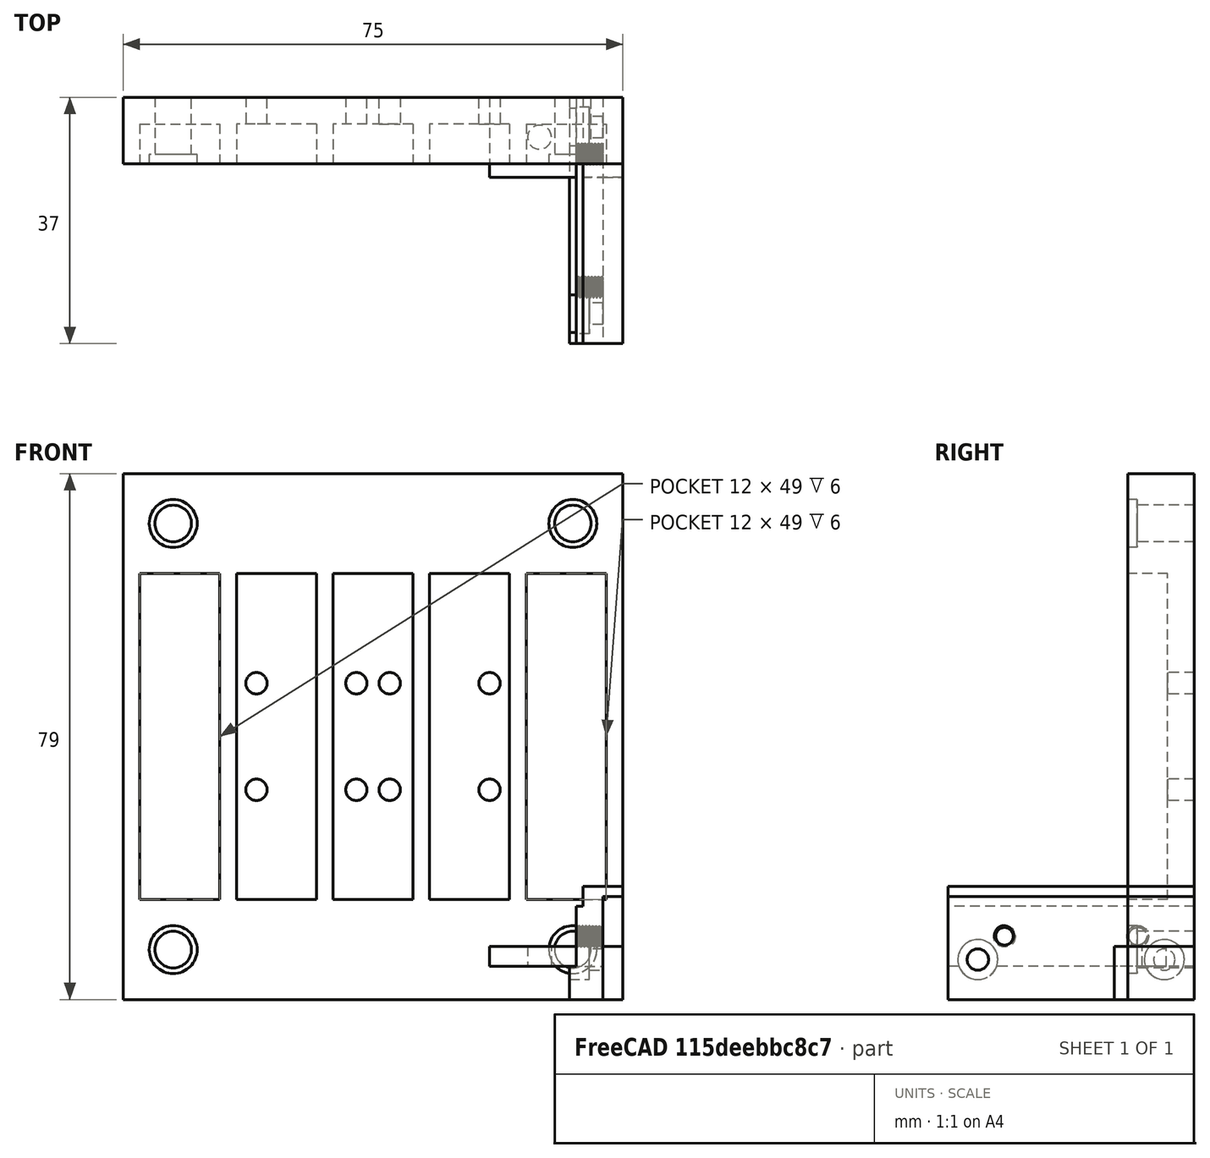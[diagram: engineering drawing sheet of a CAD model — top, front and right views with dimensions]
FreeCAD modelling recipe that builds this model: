
FCSTD DOCUMENT  (FreeCAD 0.20R29410 (Git))
Label: y_rail
License: All rights reserved
LicenseURL: http://en.wikipedia.org/wiki/All_rights_reserved
objects: Sketcher::SketchObject×12, PartDesign::Pocket×7, PartDesign::Pad×5, PartDesign::Body×3, Mesh::Feature×3, Part::FeaturePython×2, Part::Cut×2, PartDesign::Mirrored×1, PartDesign::LinearPattern×1
note: 45 computed .brp shape members not serialized (recipe doc carries the construction recipe); baked Part::Feature solids carry a one-line shape summary decoded from their .brp

FEATURE [Sketcher::SketchObject] Sketch
  FullyConstrained = true
  MapMode = 5
  Placement = pos=(0,0,0) rot=(1,0,0;1.5708rad)
  Support = -> [XZ_Plane]
  sketch-geometry (10):
    g0: LineSegment StartX=0 StartY=17 StartZ=0 EndX=0 EndY=15.5 EndZ=0
    g1: LineSegment StartX=0 StartY=15.5 StartZ=0 EndX=-3 EndY=15.5 EndZ=0
    g2: LineSegment StartX=-3 StartY=15.5 StartZ=0 EndX=-3 EndY=0 EndZ=0
    g3: LineSegment StartX=-3 StartY=0 StartZ=0 EndX=-8 EndY=0 EndZ=0
    g4: LineSegment StartX=-8 StartY=0 StartZ=0 EndX=-8 EndY=5 EndZ=0
    g5: LineSegment StartX=-8 StartY=5 StartZ=0 EndX=-7 EndY=5 EndZ=0
    g6: LineSegment StartX=-7 StartY=5 StartZ=0 EndX=-7 EndY=14 EndZ=0
    g7: LineSegment StartX=-7 StartY=14 StartZ=0 EndX=-6 EndY=14 EndZ=0
    g8: LineSegment StartX=-6 StartY=14 StartZ=0 EndX=-6 EndY=17 EndZ=0
    g9: LineSegment StartX=-6 StartY=17 StartZ=0 EndX=0 EndY=17 EndZ=0
  constraints (30):
    c: PointOnObject(g0,g-2)
    c: Vertical(g0)
    c: Coincident(g1,g0)
    c: Horizontal(g1)
    c: Coincident(g2,g1)
    c: PointOnObject(g2,g-1)
    c: Vertical(g2)
    c: Coincident(g3,g2)
    c: PointOnObject(g3,g-1)
    c: Coincident(g4,g3)
    c: Vertical(g4)
    c: Coincident(g5,g4)
    c: Horizontal(g5)
    c: Coincident(g6,g5)
    c: Vertical(g6)
    c: Coincident(g7,g6)
    c: Coincident(g8,g7)
    c: Vertical(g8)
    c: Coincident(g9,g8)
    c: Coincident(g9,g0)
    c: Horizontal(g9)
    c: DistanceY(g8,g8) = 3
    c: DistanceY(g6,g6) = 9
    c: DistanceY(g4,g4) = 5
    c: Horizontal(g7)
    c: Equal(g7,g5)
    c: DistanceX(g7,g7) = 1
    c: DistanceX(g9,g9) = 6
    c: DistanceX(g1,g1) = 3
    c: DistanceY(g0,g0) = 1.5
FEATURE [PartDesign::Pad] Pad
  Direction = (0,-1,-2e-16)
  Length = 37
  Length2 = 10
  Placement = pos=(0,0,0) rot=(1,0,0;1.5708rad)
  Profile = -> Sketch
  ReferenceAxis = -> Sketch [N_Axis]
  Type = 0
FEATURE [Sketcher::SketchObject] Sketch001
  ExternalGeometry = -> [Pad]
  FullyConstrained = true
  MapMode = 5
  Placement = pos=(-7,0,0) rot=(0.707107,0,-0.707107;3.14159rad)
  Support = -> [Pad]
  sketch-geometry (7):
    g0: Circle CenterX=-9.5 CenterY=28.5 CenterZ=0 NormalX=0 NormalY=0 NormalZ=1 AngleXU=0 Radius=1.25
    g1: Circle CenterX=-9.5 CenterY=8.5 CenterZ=0 NormalX=0 NormalY=0 NormalZ=1 AngleXU=0 Radius=1.25
    g2: LineSegment StartX=-9.5 StartY=28.5 StartZ=0 EndX=-9.5 EndY=8.5 EndZ=0
    g3: GeomPoint X=-9.5 Y=18.5 Z=0
    g4: LineSegment StartX=-14 StartY=37 StartZ=0 EndX=-5 EndY=0 EndZ=0
    g5: LineSegment StartX=-14 StartY=0 StartZ=0 EndX=-5 EndY=37 EndZ=0
    g6: GeomPoint X=-9.5 Y=18.5 Z=0
  constraints (14):
    c: Equal(g0,g1)
    c: Vertical(g0,g1)
    c: Coincident(g2,g0)
    c: Coincident(g2,g1)
    c: DistanceY(g2,g2) = 20
    c: Symmetric(g0,g1,g3)
    c: Coincident(g4,g-3)
    c: Coincident(g5,g-3)
    c: PointOnObject(g6,g5)
    c: PointOnObject(g6,g4)
    c: Coincident(g6,g3)
    c: Diameter(g0) = 2.5
    c: Coincident(g5,g-4)
    c: Coincident(g4,g-4)
FEATURE [PartDesign::Pocket] Pocket  label="table_handle_hole"
  BaseFeature = -> Pad
  Direction = (1,0,2e-16)
  Length = 5
  Length2 = 5
  Placement = pos=(0,0,0) rot=(1,0,0;1.5708rad)
  Profile = -> Sketch001
  ReferenceAxis = -> Sketch001 [N_Axis]
  Type = 1
FEATURE [Sketcher::SketchObject] Sketch002
  ExternalGeometry = -> [Pocket]
  FullyConstrained = true
  MapMode = 5
  Placement = pos=(-8,0,0) rot=(0.707107,0,-0.707107;3.14159rad)
  Support = -> [Pocket]
  sketch-geometry (5):
    g0: Circle CenterX=-6 CenterY=32.5 CenterZ=0 NormalX=0 NormalY=0 NormalZ=1 AngleXU=0 Radius=3
    g1: Circle CenterX=-6 CenterY=4.5 CenterZ=0 NormalX=0 NormalY=0 NormalZ=1 AngleXU=0 Radius=3
    g2: LineSegment StartX=-6 StartY=32.5 StartZ=0 EndX=-6 EndY=4.5 EndZ=0
    g3: GeomPoint X=-6 Y=18.5 Z=0
    g4: GeomPoint X=-5 Y=18.5 Z=0
  constraints (10):
    c: Equal(g0,g1)
    c: Coincident(g2,g0)
    c: Coincident(g2,g1)
    c: Vertical(g2)
    c: DistanceY(g2,g2) = 28
    c: Diameter(g1) = 6
    c: Symmetric(g1,g0,g3)
    c: Symmetric(g-4,g-4,g4)
    c: Horizontal(g4,g3)
    c: DistanceX(g-3,g3) = 9.5
FEATURE [PartDesign::Pocket] Pocket001  label="Y_rail_to_guide_head"
  BaseFeature = -> Pocket
  Direction = (1,0,2e-16)
  Length = 3
  Length2 = 5
  Placement = pos=(0,0,0) rot=(1,0,0;1.5708rad)
  Profile = -> Sketch002
  ReferenceAxis = -> Sketch002 [N_Axis]
  Type = 0
FEATURE [Sketcher::SketchObject] Sketch003
  ExternalGeometry = -> [Pocket001]
  FullyConstrained = true
  MapMode = 5
  Placement = pos=(-5,0,-1e-15) rot=(0.707107,0,-0.707107;3.14159rad)
  Support = -> [Pocket001]
  sketch-geometry (2):
    g0: Circle CenterX=-6 CenterY=32.5 CenterZ=0 NormalX=0 NormalY=0 NormalZ=1 AngleXU=0 Radius=1.6
    g1: Circle CenterX=-6 CenterY=4.5 CenterZ=0 NormalX=0 NormalY=0 NormalZ=1 AngleXU=0 Radius=1.6
  constraints (4):
    c: Coincident(g0,g-3)
    c: Coincident(g1,g-4)
    c: Equal(g0,g1)
    c: Diameter(g0) = 3.2
FEATURE [PartDesign::Pocket] Pocket002  label="Y_rail_to_guide"
  BaseFeature = -> Pocket001
  Direction = (1,0,2e-16)
  Length = 5
  Length2 = 5
  Placement = pos=(0,0,0) rot=(1,0,0;1.5708rad)
  Profile = -> Sketch003
  ReferenceAxis = -> Sketch003 [N_Axis]
  Type = 1
FEATURE [PartDesign::Body] Body  label="Y_rail_holder"
  Group = -> [Sketch,Pad,Sketch001,Pocket,Sketch002,Pocket001,Sketch003,Pocket002]
  Origin = -> Origin
  Tip = -> Pocket002
FEATURE [Part::FeaturePython] ScrewTap  label="M3x5-ScrewTap"  # Fasteners workbench fastener (typed FeaturePython)
  Placement = pos=(-7,-8.5,9.5) rot=(0,-1,0;1.5708rad)
  baseObject = -> Body [Edge47]
  diameter = 4
  diameterCustom = 6
  invert = false
  leftHanded = false
  length = 5
  matchOuter = false
  offset = 0
  pitchCustom = 1
  thread = true
FEATURE [Part::FeaturePython] ScrewTap001  label="M3x5-ScrewTap001"  # Fasteners workbench fastener (typed FeaturePython)
  Placement = pos=(-7,-28.5,9.5) rot=(0,-1,0;1.5708rad)
  baseObject = -> Body [Edge46]
  diameter = 4
  diameterCustom = 6
  invert = false
  leftHanded = false
  length = 5
  matchOuter = false
  offset = 0
  pitchCustom = 1
  thread = true
FEATURE [Part::Cut] Cut
  Base = -> Body
  Tool = -> ScrewTap
FEATURE [Part::Cut] Cut001  label="Y_holder_screwed"
  Base = -> Cut
  Tool = -> ScrewTap001
FEATURE [Mesh::Feature] Mesh  label="Y_holder_screwed (Meshed)"
FEATURE [Sketcher::SketchObject] Sketch008
  FullyConstrained = true
  MapMode = 5
  Placement = pos=(0,0,0) rot=(1,0,0;1.5708rad)
  Support = -> [XZ_Plane003]
  sketch-geometry (4):
    g0: LineSegment StartX=0 StartY=0 StartZ=0 EndX=-75 EndY=0 EndZ=0
    g1: LineSegment StartX=-75 StartY=0 StartZ=0 EndX=-75 EndY=79 EndZ=0
    g2: LineSegment StartX=-75 StartY=79 StartZ=0 EndX=0 EndY=79 EndZ=0
    g3: LineSegment StartX=0 StartY=79 StartZ=0 EndX=0 EndY=0 EndZ=0
  constraints (11):
    c: Coincident(g0,g1)
    c: Coincident(g1,g2)
    c: Coincident(g2,g3)
    c: Coincident(g3,g0)
    c: Horizontal(g0)
    c: Horizontal(g2)
    c: Vertical(g1)
    c: Vertical(g3)
    c: Coincident(g0,g-1)
    c: DistanceX(g2,g2) = 75
    c: DistanceY(g1,g1) = 79
FEATURE [PartDesign::Pad] Pad003  label="to_table_plate001"
  Direction = (0,-1,-2e-16)
  Length = 4
  Length2 = 10
  Placement = pos=(0,0,0) rot=(1,0,0;1.5708rad)
  Profile = -> Sketch008
  ReferenceAxis = -> Sketch008 [N_Axis]
  Type = 0
FEATURE [Sketcher::SketchObject] Sketch009
  ExternalGeometry = -> [Pad003]
  FullyConstrained = true
  MapMode = 5
  Placement = pos=(0,-4,-9e-16) rot=(1,0,0;1.5708rad)
  Support = -> [Pad003]
  sketch-geometry (8):
    g0: LineSegment StartX=-75 StartY=79 StartZ=0 EndX=0 EndY=79 EndZ=0
    g1: LineSegment StartX=0 StartY=79 StartZ=0 EndX=0 EndY=64 EndZ=0
    g2: LineSegment StartX=0 StartY=64 StartZ=0 EndX=-75 EndY=64 EndZ=0
    g3: LineSegment StartX=-75 StartY=64 StartZ=0 EndX=-75 EndY=79 EndZ=0
    g4: LineSegment StartX=-75 StartY=15 StartZ=0 EndX=0 EndY=15 EndZ=0
    g5: LineSegment StartX=0 StartY=15 StartZ=0 EndX=0 EndY=0 EndZ=0
    g6: LineSegment StartX=0 StartY=0 StartZ=0 EndX=-75 EndY=0 EndZ=0
    g7: LineSegment StartX=-75 StartY=0 StartZ=0 EndX=-75 EndY=15 EndZ=0
  constraints (20):
    c: Coincident(g0,g1)
    c: Coincident(g1,g2)
    c: Coincident(g2,g3)
    c: Coincident(g3,g0)
    c: Horizontal(g2)
    c: Vertical(g1)
    c: Vertical(g3)
    c: Coincident(g4,g5)
    c: Coincident(g5,g6)
    c: Coincident(g6,g7)
    c: Coincident(g7,g4)
    c: Horizontal(g4)
    c: Vertical(g5)
    c: Vertical(g7)
    c: Equal(g7,g3)
    c: Coincident(g0,g-3)
    c: Coincident(g0,g-3)
    c: Coincident(g6,g-4)
    c: Coincident(g5,g-4)
    c: DistanceY(g3,g3) = 15
FEATURE [PartDesign::Pad] Pad004  label="to_table_up"
  BaseFeature = -> Pad003
  Direction = (0,-1,-2e-16)
  Length = 6
  Length2 = 10
  Placement = pos=(0,0,0) rot=(1,0,0;1.5708rad)
  Profile = -> Sketch009
  ReferenceAxis = -> Sketch009 [N_Axis]
  Type = 0
FEATURE [Sketcher::SketchObject] Sketch010
  ExternalGeometry = -> [Pad004]
  FullyConstrained = true
  MapMode = 5
  Placement = pos=(0,-4,-9e-16) rot=(1,0,0;1.5708rad)
  Support = -> [Pad004]
  sketch-geometry (20):
    g0: LineSegment StartX=-55 StartY=47.5 StartZ=0 EndX=-40 EndY=47.5 EndZ=0
    g1: LineSegment StartX=-40 StartY=47.5 StartZ=0 EndX=-40 EndY=31.5 EndZ=0
    g2: LineSegment StartX=-40 StartY=31.5 StartZ=0 EndX=-55 EndY=31.5 EndZ=0
    g3: LineSegment StartX=-55 StartY=31.5 StartZ=0 EndX=-55 EndY=47.5 EndZ=0
    g4: Circle CenterX=-55 CenterY=47.5 CenterZ=0 NormalX=0 NormalY=0 NormalZ=1 AngleXU=0 Radius=1.6
    g5: Circle CenterX=-40 CenterY=47.5 CenterZ=0 NormalX=0 NormalY=0 NormalZ=1 AngleXU=0 Radius=1.6
    g6: Circle CenterX=-40 CenterY=31.5 CenterZ=0 NormalX=0 NormalY=0 NormalZ=1 AngleXU=0 Radius=1.6
    g7: Circle CenterX=-55 CenterY=31.5 CenterZ=0 NormalX=0 NormalY=0 NormalZ=1 AngleXU=0 Radius=1.6
    g8: GeomPoint X=-37.5 Y=64 Z=0
    g9: LineSegment StartX=-55 StartY=47.5 StartZ=0 EndX=-40 EndY=31.5 EndZ=0
    g10: LineSegment StartX=-40 StartY=47.5 StartZ=0 EndX=-55 EndY=31.5 EndZ=0
    g11: GeomPoint X=-47.5 Y=39.5 Z=0
    g12: LineSegment StartX=-57.5 StartY=60 StartZ=0 EndX=-37.5 EndY=60 EndZ=0
    g13: LineSegment StartX=-37.5 StartY=60 StartZ=0 EndX=-37.5 EndY=19 EndZ=0
    g14: LineSegment StartX=-37.5 StartY=19 StartZ=0 EndX=-57.5 EndY=19 EndZ=0
    g15: LineSegment StartX=-57.5 StartY=19 StartZ=0 EndX=-57.5 EndY=60 EndZ=0
    g16: LineSegment StartX=-57.5 StartY=60 StartZ=0 EndX=-37.5 EndY=19 EndZ=0
    g17: LineSegment StartX=-37.5 StartY=60 StartZ=0 EndX=-57.5 EndY=19 EndZ=0
    g18: GeomPoint X=-75 Y=39.5 Z=0
    g19: LineSegment StartX=-37.5 StartY=64 StartZ=0 EndX=-37.5 EndY=62 EndZ=0
  constraints (47):
    c: Coincident(g0,g1)
    c: Coincident(g1,g2)
    c: Coincident(g2,g3)
    c: Coincident(g3,g0)
    c: Horizontal(g0)
    c: Horizontal(g2)
    c: Vertical(g1)
    c: Vertical(g3)
    c: DistanceY(g1,g1) = 16
    c: DistanceX(g0,g0) = 15
    c: Coincident(g4,g0)
    c: Coincident(g5,g0)
    c: Coincident(g6,g1)
    c: Coincident(g7,g2)
    c: Equal(g4,g5)
    c: Equal(g5,g6)
    c: Equal(g6,g7)
    c: Diameter(g4) = 3.2
    c: Symmetric(g-7,g-7,g8)
    c: Coincident(g9,g4)
    c: Coincident(g9,g6)
    c: Coincident(g10,g5)
    c: Coincident(g10,g7)
    c: PointOnObject(g11,g9)
    c: PointOnObject(g11,g10)
    c: Coincident(g12,g13)
    c: Coincident(g13,g14)
    c: Coincident(g14,g15)
    c: Coincident(g15,g12)
    c: Horizontal(g12)
    c: Horizontal(g14)
    c: Vertical(g13)
    c: Vertical(g15)
    c: Coincident(g16,g12)
    c: Coincident(g16,g13)
    c: Coincident(g17,g12)
    c: Coincident(g17,g14)
    c: PointOnObject(g11,g16)
    c: PointOnObject(g11,g17)
    c: DistanceY(g13,g13) = 41
    c: DistanceX(g12,g12) = 20
    c: Vertical(g12,g8)
    c: Symmetric(g-8,g-8,g18)
    c: Horizontal(g11,g18)
    c: Coincident(g19,g8)
    c: Vertical(g19)
    c: DistanceY(g19,g19) = 2
FEATURE [PartDesign::Pocket] Pocket005  label="to_trail_hole"
  BaseFeature = -> Pad004
  Direction = (0,1,2e-16)
  Length = 5
  Length2 = 5
  Placement = pos=(0,0,0) rot=(1,0,0;1.5708rad)
  Profile = -> Sketch010
  ReferenceAxis = -> Sketch010 [N_Axis]
  Type = 1
FEATURE [PartDesign::Mirrored] Mirrored  label="Mirrored_to_trail_hole"
  BaseFeature = -> Pocket005
  MirrorPlane = -> Sketch010 [Axis12]
  Originals = -> [Pocket005]
  Placement = pos=(0,0,0) rot=(1,0,0;1.5708rad)
FEATURE [Sketcher::SketchObject] Sketch011
  ExternalGeometry = -> [Mirrored]
  FullyConstrained = true
  MapMode = 5
  Placement = pos=(0,-10,-2.2e-15) rot=(1,0,0;1.5708rad)
  Support = -> [Mirrored]
  sketch-geometry (13):
    g0: LineSegment StartX=-67.5 StartY=71.5 StartZ=0 EndX=-7.5 EndY=71.5 EndZ=0
    g1: LineSegment StartX=-7.5 StartY=71.5 StartZ=0 EndX=-7.5 EndY=7.5 EndZ=0
    g2: LineSegment StartX=-7.5 StartY=7.5 StartZ=0 EndX=-67.5 EndY=7.5 EndZ=0
    g3: LineSegment StartX=-67.5 StartY=7.5 StartZ=0 EndX=-67.5 EndY=71.5 EndZ=0
    g4: Circle CenterX=-67.5 CenterY=71.5 CenterZ=0 NormalX=0 NormalY=0 NormalZ=1 AngleXU=0 Radius=2.75
    g5: Circle CenterX=-7.5 CenterY=71.5 CenterZ=0 NormalX=0 NormalY=0 NormalZ=1 AngleXU=0 Radius=2.75
    g6: Circle CenterX=-7.5 CenterY=7.5 CenterZ=0 NormalX=0 NormalY=0 NormalZ=1 AngleXU=0 Radius=2.75
    g7: Circle CenterX=-67.5 CenterY=7.5 CenterZ=0 NormalX=0 NormalY=0 NormalZ=1 AngleXU=0 Radius=2.75
    g8: LineSegment StartX=-75 StartY=79 StartZ=0 EndX=0 EndY=0 EndZ=0
    g9: LineSegment StartX=0 StartY=79 StartZ=0 EndX=-75 EndY=0 EndZ=0
    g10: LineSegment StartX=-67.5 StartY=7.5 StartZ=0 EndX=-7.5 EndY=71.5 EndZ=0
    g11: LineSegment StartX=-67.5 StartY=71.5 StartZ=0 EndX=-7.5 EndY=7.5 EndZ=0
    g12: GeomPoint X=-37.5 Y=39.5 Z=0
  constraints (30):
    c: Coincident(g0,g1)
    c: Coincident(g1,g2)
    c: Coincident(g2,g3)
    c: Coincident(g3,g0)
    c: Horizontal(g0)
    c: Horizontal(g2)
    c: Vertical(g1)
    c: Vertical(g3)
    c: Coincident(g4,g0)
    c: Coincident(g5,g0)
    c: Coincident(g6,g1)
    c: Coincident(g7,g2)
    c: Equal(g4,g5)
    c: Equal(g5,g6)
    c: Equal(g6,g7)
    c: Diameter(g4) = 5.5
    c: DistanceX(g0,g0) = 60
    c: DistanceY(g3,g3) = 64
    c: Coincident(g8,g-3)
    c: Coincident(g8,g-4)
    c: Coincident(g9,g-3)
    c: Coincident(g9,g-4)
    c: Coincident(g10,g7)
    c: Coincident(g10,g5)
    c: Coincident(g11,g4)
    c: Coincident(g11,g6)
    c: PointOnObject(g12,g8)
    c: PointOnObject(g12,g11)
    c: PointOnObject(g12,g10)
    c: PointOnObject(g12,g9)
FEATURE [PartDesign::Pocket] Pocket006  label="to_table_hole"
  BaseFeature = -> Mirrored
  Direction = (0,1,2e-16)
  Length = 5
  Length2 = 5
  Placement = pos=(0,0,0) rot=(1,0,0;1.5708rad)
  Profile = -> Sketch011
  ReferenceAxis = -> Sketch011 [N_Axis]
  Type = 1
FEATURE [Sketcher::SketchObject] Sketch012
  ExternalGeometry = -> [Pocket006]
  FullyConstrained = true
  MapMode = 5
  Placement = pos=(0,-4,-9e-16) rot=(1,0,0;1.5708rad)
  Support = -> [Pocket006]
  sketch-geometry (4):
    g0: LineSegment StartX=-75 StartY=64 StartZ=0 EndX=-72.5 EndY=64 EndZ=0
    g1: LineSegment StartX=-72.5 StartY=64 StartZ=0 EndX=-72.5 EndY=15 EndZ=0
    g2: LineSegment StartX=-72.5 StartY=15 StartZ=0 EndX=-75 EndY=15 EndZ=0
    g3: LineSegment StartX=-75 StartY=15 StartZ=0 EndX=-75 EndY=64 EndZ=0
  constraints (11):
    c: Coincident(g0,g1)
    c: Coincident(g1,g2)
    c: Coincident(g2,g3)
    c: Coincident(g3,g0)
    c: Horizontal(g0)
    c: Horizontal(g2)
    c: Vertical(g1)
    c: Vertical(g3)
    c: PointOnObject(g1,g-3)
    c: DistanceX(g0,g0) = 2.5
    c: Coincident(g0,g-4)
FEATURE [PartDesign::Pad] Pad005  label="stiffener"
  BaseFeature = -> Pocket006
  Direction = (0,-1,-2e-16)
  Length = 6
  Length2 = 10
  Placement = pos=(0,0,0) rot=(1,0,0;1.5708rad)
  Profile = -> Sketch012
  ReferenceAxis = -> Sketch012 [N_Axis]
  Type = 0
FEATURE [PartDesign::LinearPattern] LinearPattern  label="stiffener_pat"
  BaseFeature = -> Pad005
  Direction = -> Sketch012 [H_Axis]
  Length = 72.5
  Occurrences = 6
  Originals = -> [Pad005]
  Placement = pos=(0,0,0) rot=(1,0,0;1.5708rad)
FEATURE [Sketcher::SketchObject] Sketch013
  FullyConstrained = true
  MapMode = 5
  Placement = pos=(0,0,0) rot=(1,0,0;1.5708rad)
  Support = -> [XZ_Plane004]
  sketch-geometry (6):
    g0: LineSegment StartX=0 StartY=0 StartZ=0 EndX=0 EndY=8 EndZ=0
    g1: LineSegment StartX=0 StartY=8 StartZ=0 EndX=-20 EndY=8 EndZ=0
    g2: LineSegment StartX=-20 StartY=8 StartZ=0 EndX=-20 EndY=5 EndZ=0
    g3: LineSegment StartX=-20 StartY=5 StartZ=0 EndX=-3 EndY=5 EndZ=0
    g4: LineSegment StartX=-3 StartY=5 StartZ=0 EndX=-3 EndY=0 EndZ=0
    g5: LineSegment StartX=-3 StartY=0 StartZ=0 EndX=0 EndY=0 EndZ=0
  constraints (17):
    c: Coincident(g0,g-1)
    c: Vertical(g0)
    c: Coincident(g1,g0)
    c: Horizontal(g1)
    c: Coincident(g2,g1)
    c: Coincident(g3,g2)
    c: Horizontal(g3)
    c: Coincident(g4,g3)
    c: PointOnObject(g4,g-1)
    c: Vertical(g4)
    c: Coincident(g5,g4)
    c: Coincident(g5,g0)
    c: Vertical(g2)
    c: Equal(g2,g5)
    c: DistanceX(g5,g5) = 3
    c: DistanceY(g0,g0) = 8
    c: DistanceX(g1,g1) = 20
FEATURE [PartDesign::Pad] Pad006  label="body"
  Direction = (0,-1,-2e-16)
  Length = 12
  Length2 = 10
  Placement = pos=(0,0,0) rot=(1,0,0;1.5708rad)
  Profile = -> Sketch013
  ReferenceAxis = -> Sketch013 [N_Axis]
  Type = 0
FEATURE [Sketcher::SketchObject] Sketch014
  ExternalGeometry = -> [Pad006]
  FullyConstrained = true
  MapMode = 5
  Placement = pos=(0,0,8) rot=(0,0,1;3.14159rad)
  Support = -> [Pad006]
  sketch-geometry (5):
    g0: Circle CenterX=12.5 CenterY=6 CenterZ=0 NormalX=0 NormalY=0 NormalZ=1 AngleXU=0 Radius=1.8
    g1: LineSegment StartX=0 StartY=0 StartZ=0 EndX=12.5 EndY=0 EndZ=0
    g2: LineSegment StartX=12.5 StartY=0 StartZ=0 EndX=12.5 EndY=6 EndZ=0
    g3: LineSegment StartX=12.5 StartY=6 StartZ=0 EndX=0 EndY=6 EndZ=0
    g4: LineSegment StartX=0 StartY=6 StartZ=0 EndX=0 EndY=0 EndZ=0
  constraints (12):
    c: Coincident(g1,g2)
    c: Coincident(g2,g3)
    c: Coincident(g3,g4)
    c: Coincident(g4,g1)
    c: Horizontal(g1)
    c: Horizontal(g3)
    c: Vertical(g2)
    c: Coincident(g1,g-1)
    c: Coincident(g2,g0)
    c: DistanceX(g3,g3) = 12.5
    c: Symmetric(g1,g-3,g3)
    c: Diameter(g0) = 3.6
FEATURE [PartDesign::Pocket] Pocket007  label="screw_hole"
  BaseFeature = -> Pad006
  Direction = (0,2e-16,-1)
  Length = 5
  Length2 = 5
  Placement = pos=(0,0,0) rot=(1,0,0;1.5708rad)
  Profile = -> Sketch014
  ReferenceAxis = -> Sketch014 [N_Axis]
  Type = 1
FEATURE [PartDesign::Body] Body004  label="Y_rail_shim"
  Group = -> [Sketch013,Pad006,Sketch014,Pocket007]
  Origin = -> Origin004
  Tip = -> Pocket007
FEATURE [Mesh::Feature] Mesh002  label="Y_rail_shim (Meshed)"
  Placement = pos=(-21,0,0) rot=(0,0,1;0rad)
FEATURE [Sketcher::SketchObject] Sketch015
  ExternalGeometry = -> [LinearPattern]
  FullyConstrained = true
  MapMode = 5
  Placement = pos=(0,-10,-2.2e-15) rot=(1,0,0;1.5708rad)
  Support = -> [LinearPattern]
  sketch-geometry (4):
    g0: Circle CenterX=-67.5 CenterY=71.5 CenterZ=0 NormalX=0 NormalY=0 NormalZ=1 AngleXU=0 Radius=3.6
    g1: Circle CenterX=-7.5 CenterY=71.5 CenterZ=0 NormalX=0 NormalY=0 NormalZ=1 AngleXU=0 Radius=3.6
    g2: Circle CenterX=-7.5 CenterY=7.5 CenterZ=0 NormalX=0 NormalY=0 NormalZ=1 AngleXU=0 Radius=3.6
    g3: Circle CenterX=-67.5 CenterY=7.5 CenterZ=0 NormalX=0 NormalY=0 NormalZ=1 AngleXU=0 Radius=3.6
  constraints (8):
    c: Coincident(g0,g-5)
    c: Coincident(g1,g-6)
    c: Coincident(g2,g-3)
    c: Coincident(g3,g-4)
    c: Equal(g3,g2)
    c: Equal(g2,g1)
    c: Equal(g1,g0)
    c: Diameter(g0) = 7.2
FEATURE [PartDesign::Pocket] Pocket008
  BaseFeature = -> LinearPattern
  Direction = (0,1,-2e-16)
  Length = 1.4
  Length2 = 5
  Placement = pos=(0,0,0) rot=(1,0,0;1.5708rad)
  Profile = -> Sketch015
  ReferenceAxis = -> Sketch015 [N_Axis]
  Type = 0
FEATURE [PartDesign::Body] Body003  label="Y_flip_guide_table_to_rail"
  Group = -> [Sketch008,Pad003,Sketch009,Pad004,Sketch010,Pocket005,Mirrored,Sketch011,Pocket006,Sketch012,Pad005,LinearPattern,Sketch015,Pocket008]
  Origin = -> Origin003
  Tip = -> Pocket008
FEATURE [Mesh::Feature] Mesh003  label="Y_flip_guide_table_to_rail (Meshed)"
  Placement = pos=(0,43,0) rot=(0,0,1;0rad)
